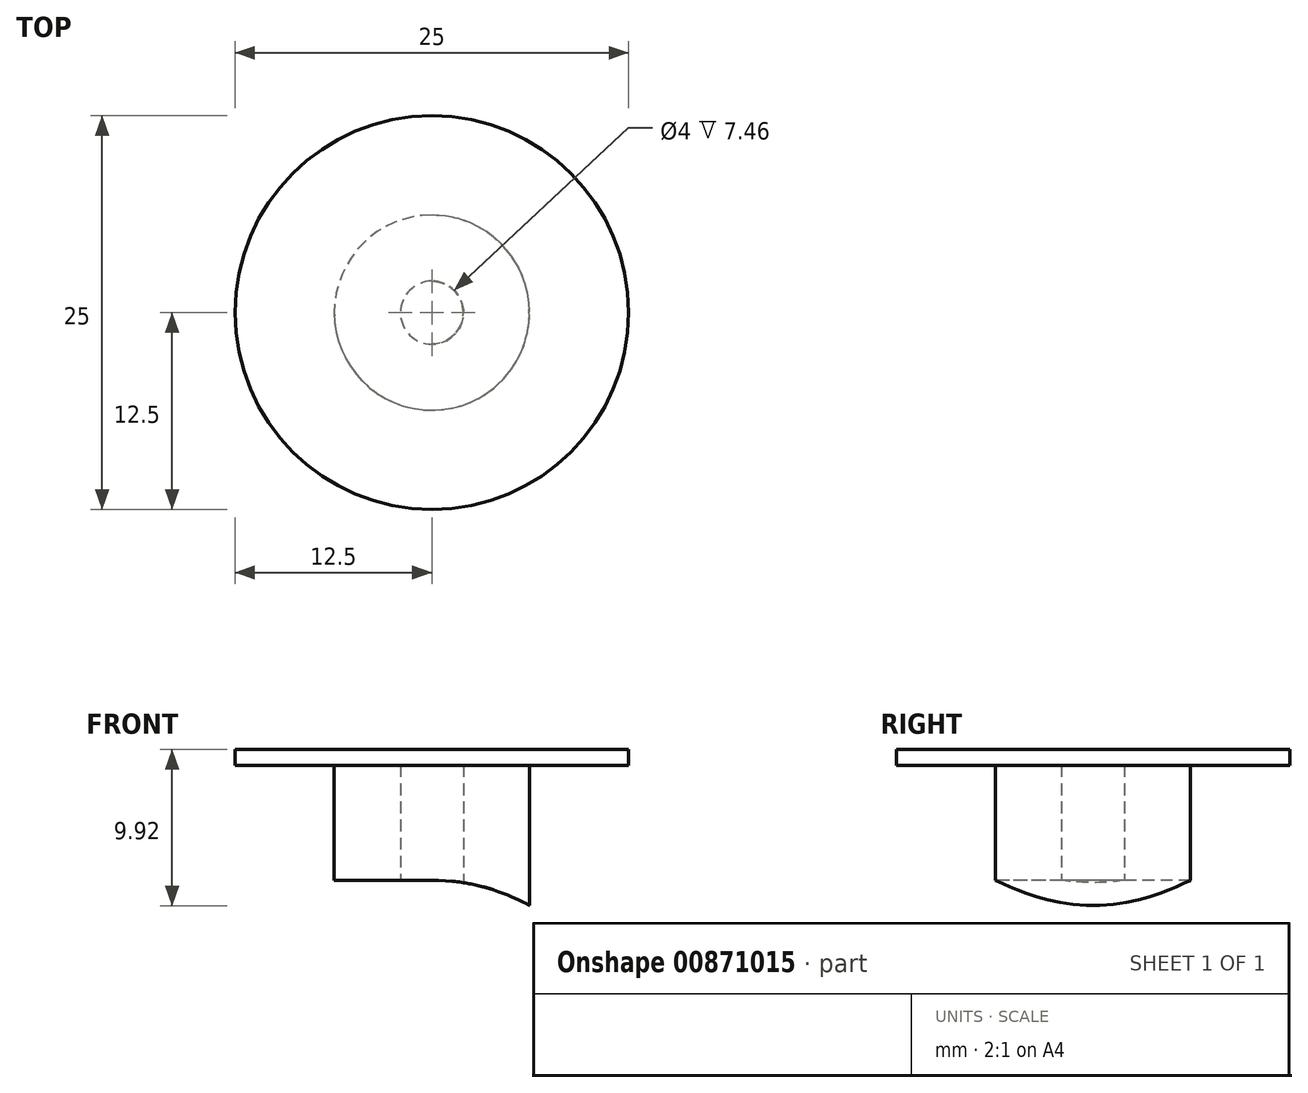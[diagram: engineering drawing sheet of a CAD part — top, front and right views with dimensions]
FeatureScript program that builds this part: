
annotation { "Feature Type Name" : "Feature", "Feature Type Description" : "" }
export const myFeature = defineFeature(function(context is Context, id is Id, definition is map)
    precondition{}
    {
        {
            var Q0;
            Q0=qCreatedBy(makeId("Top.planeOp"),FACE);
            var sketch = newSketch(context, id + "F0", { "sketchPlane" : qUnion([Q0])});
            skCircle(sketch, "E0", {"center": v(0, 0) * mm, "radius": 12.5 * mm});
            skSolve(sketch);
        }
        {
            var Q0;
            Q0 = qSketchRegion(id + "F0", true);
            extrude(context, id + "F1", {"entities" : qUnion([Q0]), "depth" : 1 * mm, "offsetDistance" : 25 * mm});
        }
        {
            var Q0;
            Q0=makeQuery(id+"F1.opExtrude","CAP_FACE",FACE,{"disambiguationData":[OSD([sQuery(id+"F0.wireOp",EDGE,"E0")])],"isStart":true});
            var sketch = newSketch(context, id + "F2", { "sketchPlane" : qUnion([Q0])});
            skCircle(sketch, "E1", {"center": v(0, 0) * mm, "radius": 6.2 * mm});
            skSolve(sketch);
        }
        {
            var Q0;
            Q0 = qSketchRegion(id + "F2", true);
            extrude(context, id + "F3", {"entities" : qUnion([Q0]), "operationType" : NewBodyOperationType.ADD, "depth" : 10 * mm, "offsetDistance" : 25 * mm});
        }
        {
            var Q0;
            Q0=qCreatedBy(makeId("Front.planeOp"),FACE);
            var sketch = newSketch(context, id + "F4", { "sketchPlane" : qUnion([Q0])});
            skPoint(sketch, "E2", {"position": v(0, -20) * mm});
            skCircle(sketch, "E3", {"center": v(0, -20) * mm, "radius": 12.7 * mm});
            skSolve(sketch);
        }
        {
            var Q0;
            Q0 = qSketchRegion(id + "F4", true);
            extrude(context, id + "F5", {"entities" : qUnion([Q0]), "operationType" : NewBodyOperationType.REMOVE, "oppositeDirection" : true, "depth" : 25 * mm, "offsetDistance" : 25 * mm, "hasSecondDirection" : true, "secondDirectionOppositeDirection" : false, "secondDirectionDepth" : 25 * mm});
        }
        {
            var Q0;
            Q0=qCreatedBy(makeId("Top.planeOp"),FACE);
            cPlane(context, id + "F6", {"entities" : qUnion([Q0]), "cplaneType" : CPlaneType.OFFSET, "offset" : 10 * mm, "oppositeDirection" : true, "width" : 150 * mm, "height" : 150 * mm});
        }
        {
            var Q0;
            Q0=qCreatedBy(id+"F6.planeOp",FACE);
            var sketch = newSketch(context, id + "F7", { "sketchPlane" : qUnion([Q0])});
            skPoint(sketch, "E4", {"position": v(0, 0) * mm});
            skCircle(sketch, "E5", {"center": v(0, 0) * mm, "radius": 2 * mm});
            skSolve(sketch);
        }
        {
            var Q0;
            Q0 = qSketchRegion(id + "F7", true);
            var Q1;
            Q1=makeQuery(id+"F1.opExtrude","CAP_FACE",FACE,{"disambiguationData":[OSD([sQuery(id+"F0.wireOp",EDGE,"E0")])],"isStart":true});
            extrude(context, id + "F8", {"entities" : qUnion([Q0]), "operationType" : NewBodyOperationType.REMOVE, "endBound" : BoundingType.UP_TO_SURFACE, "depth" : 11 * mm, "endBoundEntityFace" : qUnion([Q1]), "offsetDistance" : 25 * mm});
        }
        {
            var Q0;
            Q0=qCreatedBy(makeId("Front.planeOp"),FACE);
            var sketch = newSketch(context, id + "F9", { "sketchPlane" : qUnion([Q0])});
            skPoint(sketch, "E6", {"position": v(0, -7.3) * mm});
            skLineSegment(sketch, "E7.bottom", {"start": v(0, -7.3) * mm, "end": v(-9.56, -7.3) * mm});
            skLineSegment(sketch, "E7.top", {"start": v(0, -11.2) * mm, "end": v(-9.56, -11.2) * mm});
            skLineSegment(sketch, "E7.left", {"start": v(0, -7.3) * mm, "end": v(0, -11.2) * mm});
            skLineSegment(sketch, "E7.right", {"start": v(-9.56, -7.3) * mm, "end": v(-9.56, -11.2) * mm});
            skSolve(sketch);
        }
        {
            var Q0;
            Q0 = qSketchRegion(id + "F9", true);
            extrude(context, id + "F10", {"entities" : qUnion([Q0]), "operationType" : NewBodyOperationType.REMOVE, "endBound" : BoundingType.THROUGH_ALL, "oppositeDirection" : true, "depth" : 25 * mm, "offsetDistance" : 25 * mm, "hasSecondDirection" : true, "secondDirectionBound" : BoundingType.THROUGH_ALL, "secondDirectionOppositeDirection" : false, "secondDirectionDepth" : 25 * mm});
        }
    });
